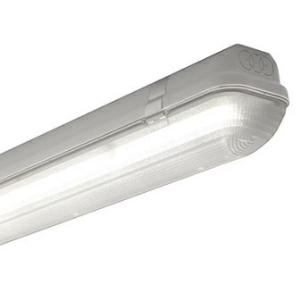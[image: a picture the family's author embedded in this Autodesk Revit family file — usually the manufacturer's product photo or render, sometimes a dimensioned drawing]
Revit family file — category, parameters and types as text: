
# Revit family: 3f_filippi_-_3f_linda_3f_filippi_-_58608_-_3f_linda_led_1x22w_l1570
name_source: partatom
category: Lighting Fixtures
units: mm (PartAtom-declared; Revit-internal decimal feet)

## family parameters
Cut with Voids When Loaded = No
Host = Face
Light Source = No
Part Type = Normal
Room Calculation Point = No
Round Connector Dimension = Use Diameter
Shared = No

## types (1)
- 3F Filippi - 3F Linda (1 x LED, 3955 lm, 25 W, 4000 K)
    Apparent Load = 25 VA
    Approval mark = CE
    CIE Flux Codes = 44 77 94 97 100
    Color Rendering = 80
    Color Temperature = 4000 K
    Control Gear = Electronic ballast
    Default Elevation = 1800 mm
    Description = ILLUMINOTECHNICAL
Luminous efficiency 100% (DLOR 97%, ULOR 3%).
Initial luminous flux of the luminaire 3955 lm.
Controlled symmetric distribution.
Installation Interdistance Transv.D = 1.77 x hu - Long.D = 1.17 x hu.
Tabular UGR (CIE 117 - 4H-8H; S=0.25H; 70/50/20): RUG 21.1 - 22.1.
Beam angle: 109° - 64°.
Luminous efficacy 158 lm/W.
Lifetime (L93/B10): 30000 h. (tq+25°C)
Lifetime (L90/B10): 50000 h. (tq+25°C)
Lifetime (L85/B10): 80000 h. (tq+25°C)
Lifetime (L80/B10): 100000 h. (tq+25°C)
Lifetime (L85/B10): 50000 h. (tq+40°C)
Sudden decreased luminous flux after 50000 hours: 0% (C0).
Photobiological safety in compliance with IEC/TR 62778: RG0 risk exempt, (IEC 62471).
In compliance with IEC/EN 62722-2-1 - IEC/EN 62717 standards.

SOURCE
Linear LED module 22W/840.
Energy efficiency class (UE 2019/2020 - UE 2019/2015): D.
CIE 13.3 Colour rendering index: CRI >80 (R9 <50%).
IES TM-30 Fidelity Index: Rf = 84 Rg = 95.
CCT nominal colour temperature 4000 K.
Colour initial tolerance (MacAdam): SDCM 3.

MECHANICAL
Self-extinguishing V2 polycarbonate housing, injection moulded, RAL 7035 grey.
Ecologic anti-aging injected sealing gasket.
Diffuser in self-extinguishing V2 polycarbonate, photo-engraved interior, UV stabilised, injection moulded with smooth outer surface, tamper-proof opening.
Gear-holder reflector in hot-dip galvanised steel, painted with white polyester base.
Snug fit safety snap-lock clips for diffuser mounting in stainless steel, screwdriver opening.
Fixing brackets in stainless steel.
Possibility for technicians to access the interior of the luminaire.
Luminaire with limited surface temperature. - D - (EN 60598-2-24)
Dimensions: 1570x100 mm, height 100 mm. Weight 2.67 kg.
IP66 protection degree.
Mechanical strength to impacts IK10 (20 joule).
Glow-wire test resistance 850°C.

ELECTRICAL
Halogen Free electronic wiring 230V-50/60Hz, power factor 0.90, THD <25%, constant output current, SELV, class I, 1 driver.
Power of the luminaire 25 W.
ENEC - CE.
SAFE FLICKER: PstLM=<1 and SVM=<0.4 (IEC TR 61547-1 and IEC TR 63158), to ensure a more comfortable and safe light.
Luminaire compliant with EN 60598-2-22 for power supply from a centralised emergency system CPSS (Central Power Supply System), not incorporated in the luminaire - high risk areas excluded. The default power and flux are 100% in AC and 100% in DC.
Ambient temperature from -20°C to +40°C.
Temperature class T6 max 85°C.
Relative humidity UR: <85%.

INSTALLATION
Ceiling / Suspended / Wall.
All accessories dedicated to this product are available on the Catalog and on our website www.3F-Filippi.com.

APPLICATIONS
Suitable product for food production plants (HACCP), IFS (Food Version 6), BRC (GSFS Food Version 7).
Dry, dusty indoor environments, subject to occasional water splashes.
Virtually shatterproof polycarbonate compatibly with the fumes / atmospheres that compromise the elasticity of plastic materials.
Not suitable for installation on surfaces subject to important vibrations, exposed to weather conditions, on ropes or poles.
Suitable for illumination of public car parks and parking grounds referred to DIN 67528:2018-04.

WARNING
Fixture not suitable for cold stores with an ambient temperature <0°C and/or relative humidity >85%.
Luminaire designed for disposal/recycling at end-of-life.
Replaceable (LED only) light source by a professional. Replaceable control gear by a professional.
    Height = 100 mm  [stored 0.328084 ft]
    Lamp = 1 x LED
    Lamp Light Flux = 3955 lm
    Lamp Power = 25 W
    Lamp count = 1
    Length = 1570 mm
    Lifetime = 50000 h
    Luminous efficacy = 158 lm/W
    Manufacturer = 3F Filippi
    ModVariant = No
    Model = 3F Filippi - 58608 - 3F Linda LED 1x22W L1570
    Mounting Place = Ceiling
    Mounting Type = Pendant
    Number of Poles = 1
    OnlyDefault = Yes
    Power Factor = 1
    Product Name = 3F Filippi - 3F Linda
    Product group = pendant luminaire
    ProductGroupID = 9
    Protection Class = Protection class I
    Protection Degree = IP 66
    RLX_Detail_Level = 1
    RLX_Emergency_Light_Flux = 0 lm
    RLX_Emergency_Type = 0
    RLX_Emergency_Type_DB = No
    RlxData = <blob elided: 68729 chars, md5=5fdb77cc>
    Socket = socket
    Standby Power = 0 W
    System Light Flux = 3955 lm
    System Power = 25 W
    Type Comments = Product without accessories
    Type Image = 3ffilippi_3f_linda_led_1x.jpg
    URL = http://relux.com
    VarID = ---
    Voltage = 0 V
    Weight = 0.00 kg
    Width = 100 mm  [stored 0.328084 ft]

note: [stored X ft] marks values corroborated as IEEE doubles in the binary element streams (Revit-internal decimal feet)

## geometry (parser evidence)
native form markers: Blend x4, Sweep x11
no freeform markers — native parametric forms only
